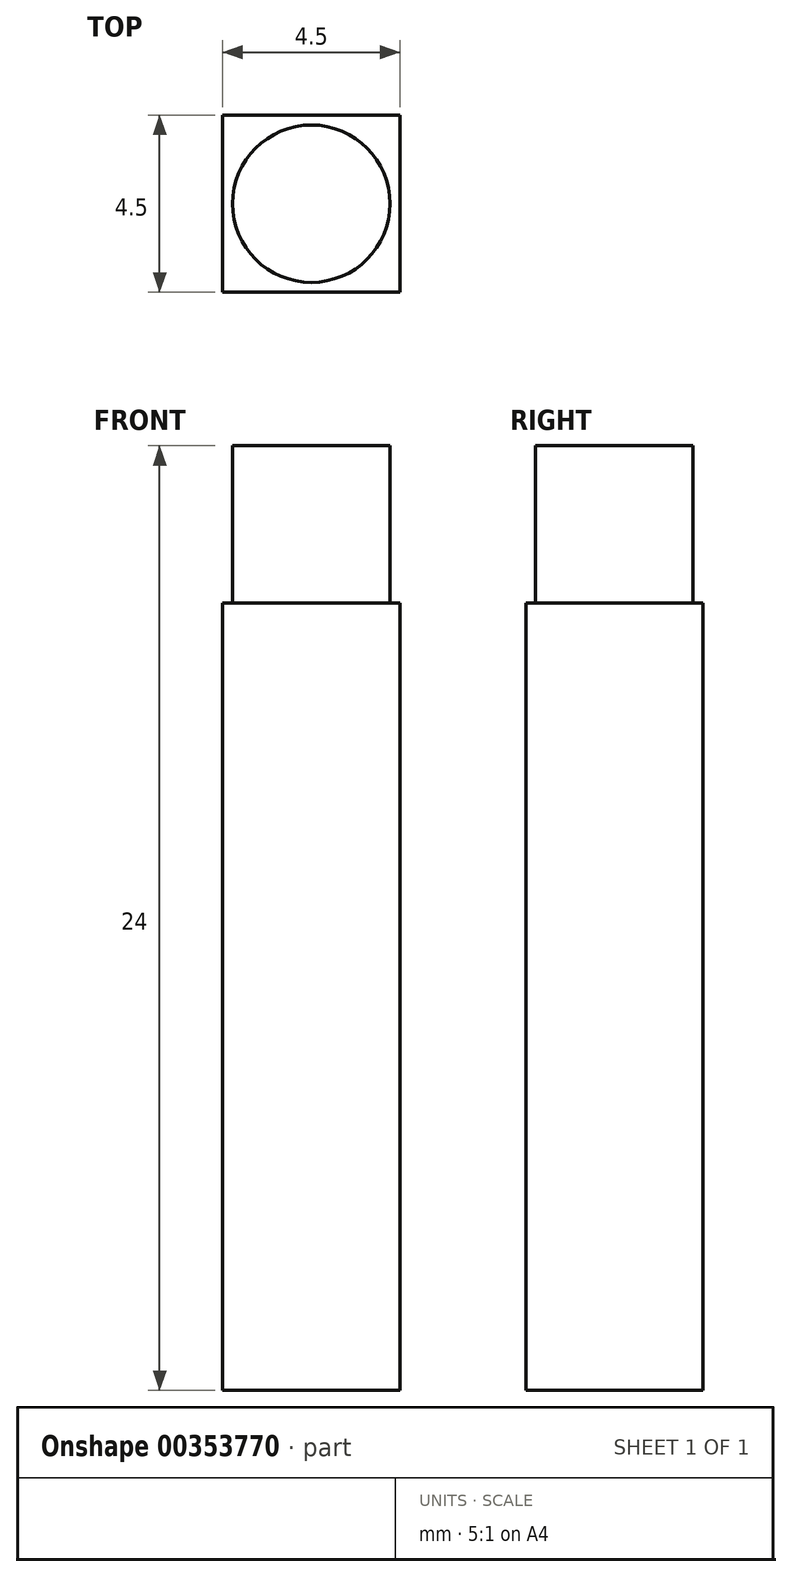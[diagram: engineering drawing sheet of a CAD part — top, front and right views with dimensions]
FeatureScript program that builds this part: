
annotation { "Feature Type Name" : "Feature", "Feature Type Description" : "" }
export const myFeature = defineFeature(function(context is Context, id is Id, definition is map)
    precondition{}
    {
        {
            var Q0;
            Q0=qCreatedBy(makeId("Top.planeOp"),FACE);
            var sketch = newSketch(context, id + "F0", { "sketchPlane" : qUnion([Q0])});
            skLineSegment(sketch, "E0.bottom", {"start": v(0, 0) * mm, "end": v(4.5, 0) * mm});
            skLineSegment(sketch, "E0.top", {"start": v(0, 4.5) * mm, "end": v(4.5, 4.5) * mm});
            skLineSegment(sketch, "E0.left", {"start": v(0, 0) * mm, "end": v(0, 4.5) * mm});
            skLineSegment(sketch, "E0.right", {"start": v(4.5, 0) * mm, "end": v(4.5, 4.5) * mm});
            skSolve(sketch);
        }
        {
            var Q0;
            Q0=makeQuery(id+"F0.imprint","IMPRINT",FACE,{"disambiguationData":[TD([[makeQuery(id+"F0.imprint","IMPRINT",EDGE,{"derivedFrom":sQuery(id+"F0.wireOp",EDGE,"E0.bottom")}),1.0]])]});
            extrude(context, id + "F1", {"entities" : qUnion([Q0]), "depth" : 20 * mm});
        }
        {
            var Q0;
            Q0=makeQuery(id+"F1.opExtrude","CAP_FACE",FACE,{"disambiguationData":[OSD([sQuery(id+"F0.wireOp",EDGE,"E0.bottom"),sQuery(id+"F0.wireOp",EDGE,"E0.top"),sQuery(id+"F0.wireOp",EDGE,"E0.left"),sQuery(id+"F0.wireOp",EDGE,"E0.right")])],"isStart":false});
            var sketch = newSketch(context, id + "F2", { "sketchPlane" : qUnion([Q0])});
            skLineSegment(sketch, "E1", {"start": v(0, 2.25) * mm, "end": v(4.5, 2.25) * mm});
            skLineSegment(sketch, "E2", {"start": v(4.5, 2.25) * mm, "end": v(2.25, 4.5) * mm, "construction": true});
            skLineSegment(sketch, "E3", {"start": v(2.25, 4.5) * mm, "end": v(2.25, 0) * mm});
            skCircle(sketch, "E4", {"center": v(2.25, 2.25) * mm, "radius": 2 * mm});
            skSolve(sketch);
        }
        {
            var Q0;
            {var subQ0=sQuery(id+"F2.wireOp",EDGE,"E4");var subQ1=sQuery(id+"F2.wireOp",EDGE,"E1");var subQ2=makeQuery(id+"F2.imprint","INTERSECT",VERTEX,{"disambiguationData":[OD(0.0)],"derivedFrom":[subQ1,subQ0]});Q0=makeQuery(id+"F2.imprint","IMPRINT",FACE,{"disambiguationData":[TD([[makeQuery(id+"F2.imprint","IMPRINT",EDGE,{"disambiguationData":[TD([[subQ2,-1.0]])],"derivedFrom":subQ1}),1.0]])]});}
            var Q1;
            {var subQ0=sQuery(id+"F2.wireOp",EDGE,"E3");var subQ1=sQuery(id+"F2.wireOp",EDGE,"E1");var subQ2=makeQuery(id+"F2.imprint","INTERSECT",VERTEX,{"derivedFrom":[subQ1,subQ0]});Q1=makeQuery(id+"F2.imprint","IMPRINT",FACE,{"disambiguationData":[TD([[makeQuery(id+"F2.imprint","IMPRINT",EDGE,{"disambiguationData":[TD([[subQ2,-1.0]])],"derivedFrom":subQ1}),1.0]])]});}
            var Q2;
            {var subQ0=sQuery(id+"F2.wireOp",EDGE,"E3");var subQ1=sQuery(id+"F2.wireOp",EDGE,"E1");var subQ2=makeQuery(id+"F2.imprint","INTERSECT",VERTEX,{"derivedFrom":[subQ1,subQ0]});Q2=makeQuery(id+"F2.imprint","IMPRINT",FACE,{"disambiguationData":[TD([[makeQuery(id+"F2.imprint","IMPRINT",EDGE,{"disambiguationData":[TD([[subQ2,-1.0]])],"derivedFrom":subQ1}),-1.0]])]});}
            var Q3;
            {var subQ0=sQuery(id+"F2.wireOp",EDGE,"E4");var subQ1=sQuery(id+"F2.wireOp",EDGE,"E1");var subQ2=makeQuery(id+"F2.imprint","INTERSECT",VERTEX,{"disambiguationData":[OD(0.0)],"derivedFrom":[subQ1,subQ0]});Q3=makeQuery(id+"F2.imprint","IMPRINT",FACE,{"disambiguationData":[TD([[makeQuery(id+"F2.imprint","IMPRINT",EDGE,{"disambiguationData":[TD([[subQ2,-1.0]])],"derivedFrom":subQ1}),-1.0]])]});}
            extrude(context, id + "F3", {"entities" : qUnion([Q0, Q1, Q2, Q3]), "operationType" : NewBodyOperationType.ADD, "depth" : 4 * mm});
        }
    });
